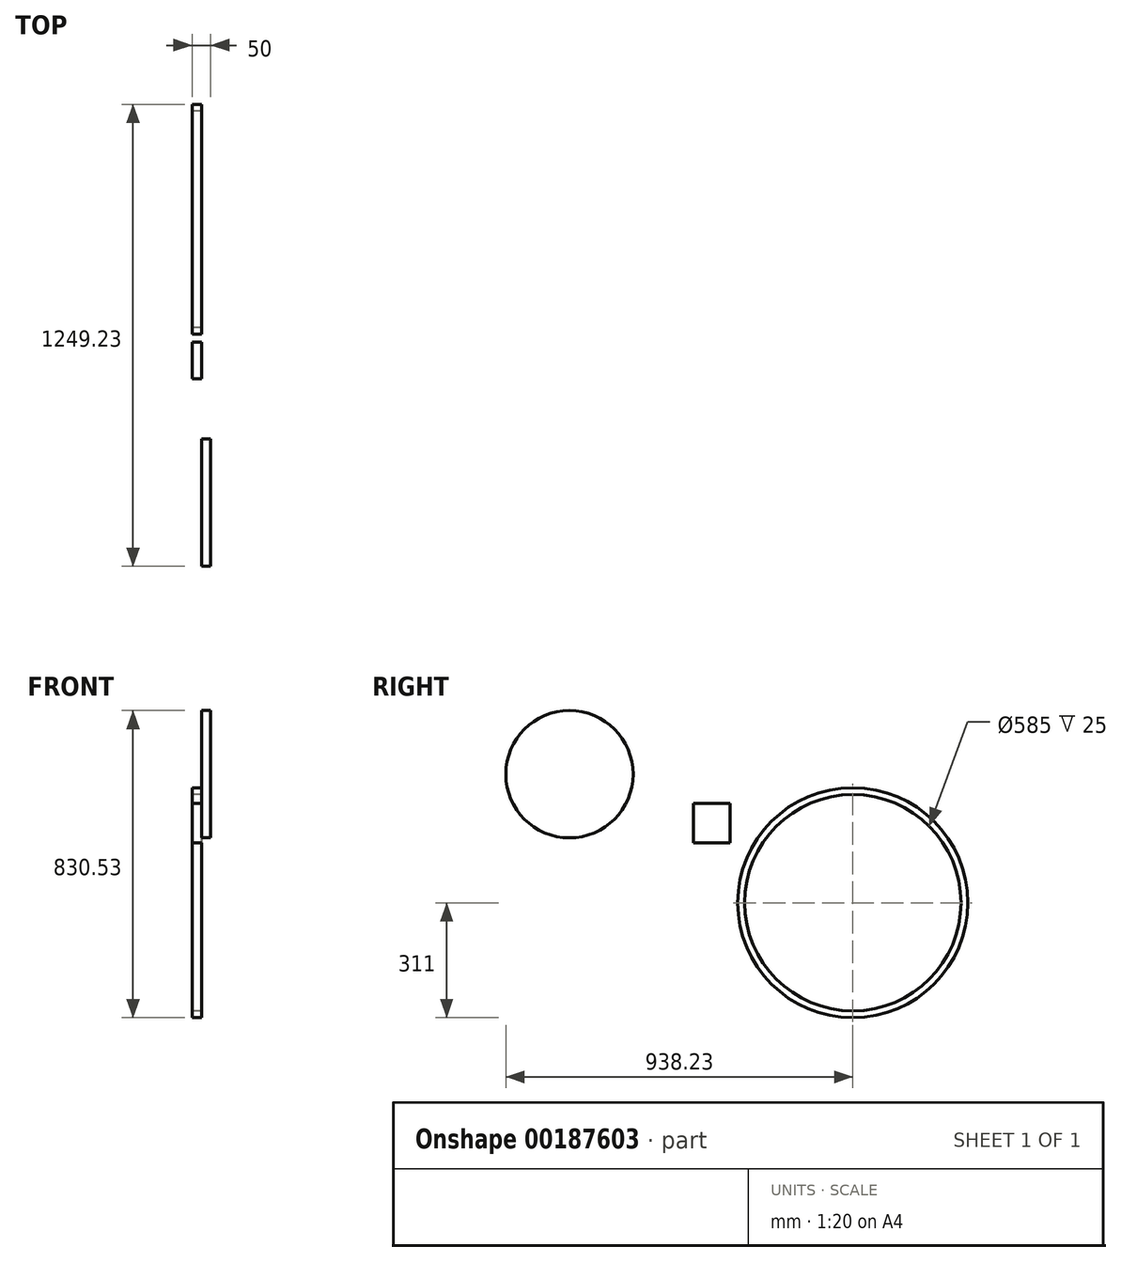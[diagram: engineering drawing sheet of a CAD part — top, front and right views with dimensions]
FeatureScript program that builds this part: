
annotation { "Feature Type Name" : "Feature", "Feature Type Description" : "" }
export const myFeature = defineFeature(function(context is Context, id is Id, definition is map)
    precondition{}
    {
        {
            var Q0;
            Q0=qCreatedBy(makeId("Right.planeOp"),FACE);
            var sketch = newSketch(context, id + "F0", { "sketchPlane" : qUnion([Q0])});
            skCircle(sketch, "E0", {"center": v(0, 0) * mm, "radius": 311 * mm});
            skSolve(sketch);
        }
        {
            var Q0;
            Q0=makeQuery(id+"F0.imprint","IMPRINT",FACE,{"disambiguationData":[TD([[makeQuery(id+"F0.imprint","IMPRINT",EDGE,{"derivedFrom":sQuery(id+"F0.wireOp",EDGE,"E0")}),1.0]])]});
            var sketch = newSketch(context, id + "F1", { "sketchPlane" : qUnion([Q0])});
            skCircle(sketch, "E1", {"center": v(0, 0) * mm, "radius": 292.5 * mm});
            skSolve(sketch);
        }
        {
            var Q0;
            Q0=sQuery(id+"F0.wireOp",EDGE,"E0");
            extrude(context, id + "F2", {"bodyType" : ToolBodyType.SURFACE, "surfaceEntities" : qUnion([Q0]), "depth" : 25 * mm});
        }
        {
            var Q0;
            Q0=makeQuery(id+"F1.imprint","IMPRINT",FACE,{"disambiguationData":[TD([[makeQuery(id+"F1.imprint","IMPRINT",EDGE,{"derivedFrom":sQuery(id+"F1.wireOp",EDGE,"E1")}),-1.0]])]});
            extrude(context, id + "F3", {"entities" : qUnion([Q0]), "depth" : 25 * mm});
        }
        {
            var Q0;
            Q0=makeQuery(id+"F2.opExtrude","SWEPT_BODY",BODY,{"disambiguationData":[OSD([sQuery(id+"F0.wireOp",EDGE,"E0")])]});
            deleteBodies(context, id + "F4", {"entities" : qUnion([Q0])});
        }
        {
            var Q0;
            Q0=qCreatedBy(makeId("Right.planeOp"),FACE);
            var sketch = newSketch(context, id + "F5", { "sketchPlane" : qUnion([Q0])});
            skLineSegment(sketch, "E2.bottom", {"start": v(-431.17, 162.18) * mm, "end": v(-331.95, 162.18) * mm});
            skLineSegment(sketch, "E2.top", {"start": v(-431.17, 268.57) * mm, "end": v(-331.95, 268.57) * mm});
            skLineSegment(sketch, "E2.left", {"start": v(-431.17, 162.18) * mm, "end": v(-431.17, 268.57) * mm});
            skLineSegment(sketch, "E2.right", {"start": v(-331.95, 162.18) * mm, "end": v(-331.95, 268.57) * mm});
            skSolve(sketch);
        }
        {
            var Q0;
            Q0=makeQuery(id+"F5.imprint","IMPRINT",FACE,{"disambiguationData":[TD([[makeQuery(id+"F5.imprint","IMPRINT",EDGE,{"derivedFrom":sQuery(id+"F5.wireOp",EDGE,"E2.bottom")}),1.0]])]});
            extrude(context, id + "F6", {"entities" : qUnion([Q0]), "depth" : 25 * mm});
        }
        {
            var Q0;
            Q0=makeQuery(id+"F6.opExtrude","CAP_FACE",FACE,{"disambiguationData":[OSD([sQuery(id+"F5.wireOp",EDGE,"E2.bottom"),sQuery(id+"F5.wireOp",EDGE,"E2.top"),sQuery(id+"F5.wireOp",EDGE,"E2.left"),sQuery(id+"F5.wireOp",EDGE,"E2.right")])],"isStart":false});
            var sketch = newSketch(context, id + "F7", { "sketchPlane" : qUnion([Q0])});
            skCircle(sketch, "E3", {"center": v(-766.14, 347.44) * mm, "radius": 172.09 * mm});
            skSolve(sketch);
        }
        {
            var Q0;
            Q0=makeQuery(id+"F7.imprint","IMPRINT",FACE,{"disambiguationData":[TD([[makeQuery(id+"F7.imprint","IMPRINT",EDGE,{"derivedFrom":sQuery(id+"F7.wireOp",EDGE,"E3")}),1.0]])]});
            extrude(context, id + "F8", {"entities" : qUnion([Q0]), "depth" : 25 * mm});
        }
    });
